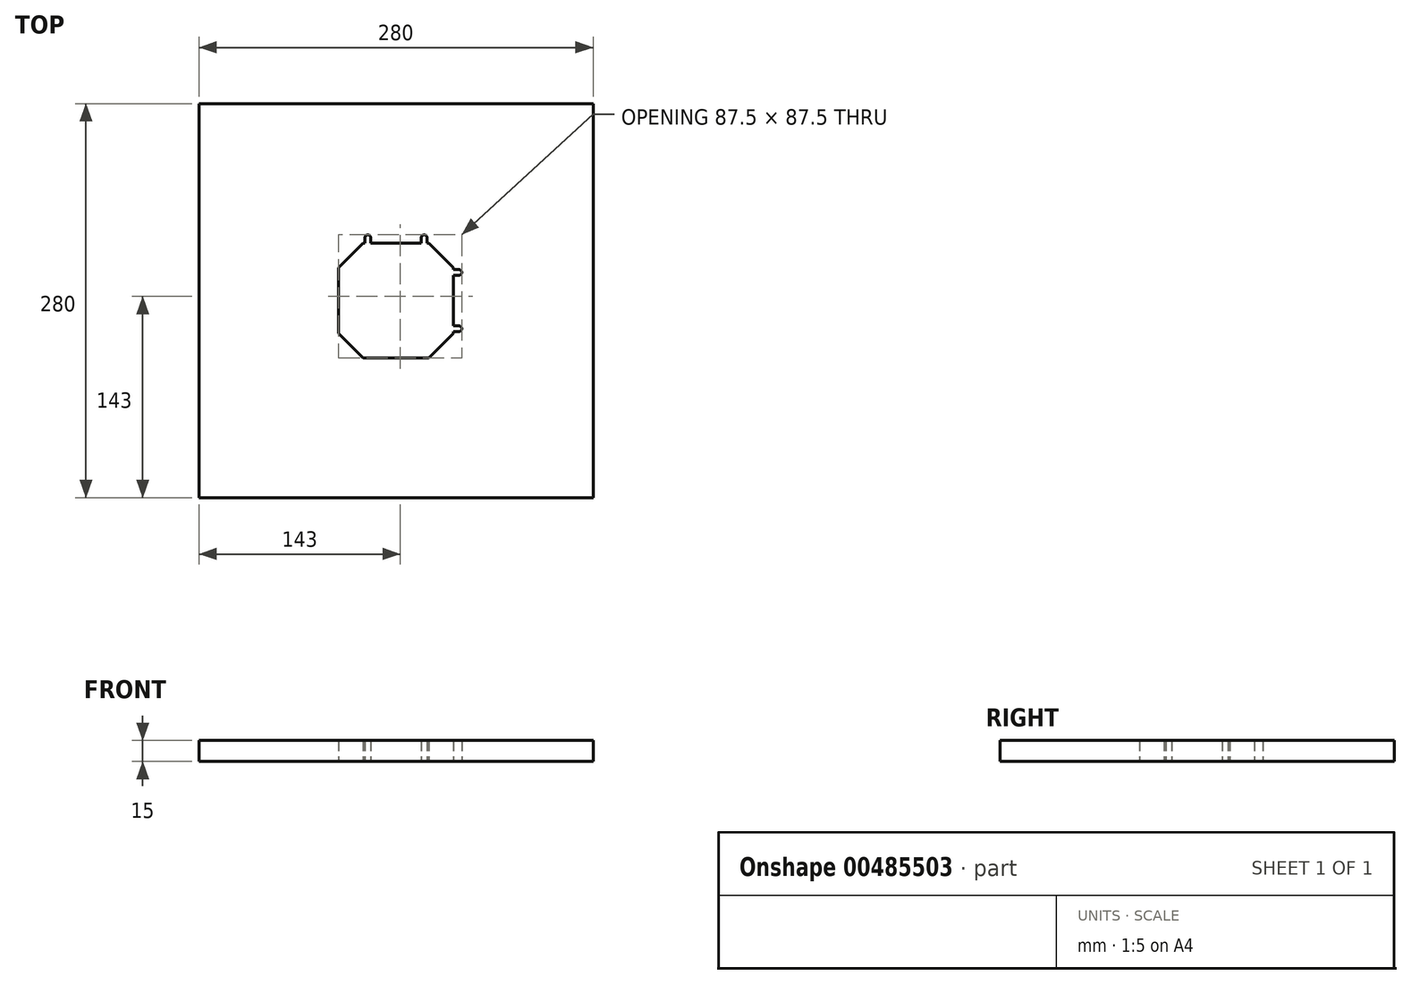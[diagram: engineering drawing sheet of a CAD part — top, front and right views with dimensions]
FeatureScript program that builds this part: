
annotation { "Feature Type Name" : "Feature", "Feature Type Description" : "" }
export const myFeature = defineFeature(function(context is Context, id is Id, definition is map)
    precondition{}
    {
        {
            var Q0;
            Q0=qCreatedBy(makeId("Top.planeOp"),FACE);
            var sketch = newSketch(context, id + "F0", { "sketchPlane" : qUnion([Q0])});
            skLineSegment(sketch, "E0.bottom", {"start": v(-140, 140) * mm, "end": v(140, 140) * mm});
            skLineSegment(sketch, "E0.top", {"start": v(-140, -140) * mm, "end": v(140, -140) * mm});
            skLineSegment(sketch, "E0.left", {"start": v(-140, 140) * mm, "end": v(-140, -140) * mm});
            skLineSegment(sketch, "E0.right", {"start": v(140, 140) * mm, "end": v(140, -140) * mm});
            skPoint(sketch, "E0.middle", {"position": v(0, 0) * mm});
            skSolve(sketch);
        }
        {
            var Q0;
            Q0 = qSketchRegion(id + "F0", true);
            extrude(context, id + "F1", {"entities" : qUnion([Q0]), "depth" : 15 * mm});
        }
        {
            var Q0;
            Q0=qCreatedBy(makeId("Top.planeOp"),FACE);
            var sketch = newSketch(context, id + "F2", { "sketchPlane" : qUnion([Q0])});
            skLineSegment(sketch, "E1.bottom", {"start": v(-40.75, 40.75) * mm, "end": v(40.75, 40.75) * mm, "construction": true});
            skLineSegment(sketch, "E1.top", {"start": v(-40.75, -40.75) * mm, "end": v(40.75, -40.75) * mm, "construction": true});
            skLineSegment(sketch, "E1.left", {"start": v(-40.75, 40.75) * mm, "end": v(-40.75, -40.75) * mm, "construction": true});
            skLineSegment(sketch, "E1.right", {"start": v(40.75, 40.75) * mm, "end": v(40.75, -40.75) * mm, "construction": true});
            skPoint(sketch, "E1.middle", {"position": v(0, 0) * mm});
            skSolve(sketch);
        }
        {
            var Q0;
            Q0=qCreatedBy(makeId("Top.planeOp"),FACE);
            var sketch = newSketch(context, id + "F3", { "sketchPlane" : qUnion([Q0])});
            skLineSegment(sketch, "E2", {"start": v(-40.75, 0) * mm, "end": v(-40.75, 23.25) * mm});
            skLineSegment(sketch, "E3", {"start": v(-40.75, 23.25) * mm, "end": v(-23.25, 40.75) * mm});
            skLineSegment(sketch, "E4", {"start": v(-23.25, 40.75) * mm, "end": v(-22, 40.75) * mm});
            skLineSegment(sketch, "E5", {"start": v(0, 40.75) * mm, "end": v(18, 40.75) * mm});
            skLineSegment(sketch, "E6", {"start": v(23.25, 40.75) * mm, "end": v(40.75, 23.25) * mm});
            skLineSegment(sketch, "E7", {"start": v(40.75, 23.25) * mm, "end": v(40.75, 22) * mm});
            skLineSegment(sketch, "E8", {"start": v(40.75, 0) * mm, "end": v(40.75, -18) * mm});
            skLineSegment(sketch, "E9", {"start": v(40.75, -23.25) * mm, "end": v(23.25, -40.75) * mm});
            skLineSegment(sketch, "E10", {"start": v(23.25, -40.75) * mm, "end": v(0, -40.75) * mm});
            skLineSegment(sketch, "E11", {"start": v(0, -40.75) * mm, "end": v(-23.25, -40.75) * mm});
            skLineSegment(sketch, "E12", {"start": v(-23.25, -40.75) * mm, "end": v(-40.75, -23.25) * mm});
            skLineSegment(sketch, "E13", {"start": v(-40.75, -23.25) * mm, "end": v(-40.75, 0) * mm});
            skLineSegment(sketch, "E14.left", {"start": v(-22, 44.75) * mm, "end": v(-22, 40.75) * mm});
            skLineSegment(sketch, "E14.right", {"start": v(-18, 44.75) * mm, "end": v(-18, 40.75) * mm});
            skPoint(sketch, "E14.middle", {"position": v(-20, 40.75) * mm});
            skLineSegment(sketch, "E15.left", {"start": v(18, 44.75) * mm, "end": v(18, 40.75) * mm});
            skLineSegment(sketch, "E15.right", {"start": v(22, 44.75) * mm, "end": v(22, 40.75) * mm});
            skPoint(sketch, "E15.middle", {"position": v(20, 40.75) * mm});
            skPoint(sketch, "E15.cornerSnap0", {"position": v(-20, 44.75) * mm});
            skArc(sketch, "E16", {"start": v(-18, 44.75) * mm, "mid": v(-20, 46.75) * mm, "end": v(-22, 44.75) * mm});
            skArc(sketch, "E17", {"start": v(22, 44.75) * mm, "mid": v(20, 46.75) * mm, "end": v(18, 44.75) * mm});
            skLineSegment(sketch, "E18.trimOffspring", {"start": v(-18, 40.75) * mm, "end": v(0, 40.75) * mm});
            skLineSegment(sketch, "E19.trimOffspring", {"start": v(22, 40.75) * mm, "end": v(23.25, 40.75) * mm});
            skLineSegment(sketch, "E20.bottom", {"start": v(44.75, 22) * mm, "end": v(40.75, 22) * mm});
            skLineSegment(sketch, "E20.top", {"start": v(44.75, 18) * mm, "end": v(40.75, 18) * mm});
            skPoint(sketch, "E20.middle", {"position": v(40.75, 20) * mm});
            skLineSegment(sketch, "E21.bottom", {"start": v(44.75, -22) * mm, "end": v(40.75, -22) * mm});
            skLineSegment(sketch, "E21.top", {"start": v(44.75, -18) * mm, "end": v(40.75, -18) * mm});
            skPoint(sketch, "E21.middle", {"position": v(40.75, -20) * mm});
            skArc(sketch, "E22", {"start": v(44.75, 18) * mm, "mid": v(46.75, 20) * mm, "end": v(44.75, 22) * mm});
            skArc(sketch, "E23", {"start": v(44.75, -22) * mm, "mid": v(46.75, -20) * mm, "end": v(44.75, -18) * mm});
            skLineSegment(sketch, "E24.trimOffspring", {"start": v(40.75, -22) * mm, "end": v(40.75, -23.25) * mm});
            skPoint(sketch, "E21.right.end.orphan", {"position": v(36.75, -18) * mm});
            skPoint(sketch, "E25.orphan", {"position": v(36.75, -22) * mm});
            skPoint(sketch, "E26.orphan", {"position": v(36.75, 22) * mm});
            skPoint(sketch, "E27.orphan", {"position": v(36.75, 18) * mm});
            skLineSegment(sketch, "E28.trimOffspring", {"start": v(40.75, 18) * mm, "end": v(40.75, 0) * mm});
            skSolve(sketch);
        }
        {
            var Q0;
            Q0 = qSketchRegion(id + "F3", true);
            extrude(context, id + "F4", {"entities" : qUnion([Q0]), "operationType" : NewBodyOperationType.REMOVE, "endBound" : BoundingType.THROUGH_ALL, "depth" : 25 * mm});
        }
        {
            var Q0;
            Q0=makeQuery(id+"F1.opExtrude","CAP_FACE",FACE,{"disambiguationData":[OSD([sQuery(id+"F0.wireOp",EDGE,"E0.bottom"),sQuery(id+"F0.wireOp",EDGE,"E0.top"),sQuery(id+"F0.wireOp",EDGE,"E0.left"),sQuery(id+"F0.wireOp",EDGE,"E0.right")])],"isStart":false});
            var sketch = newSketch(context, id + "F5", { "sketchPlane" : qUnion([Q0])});
            skLineSegment(sketch, "E29.bottom", {"start": v(42, 42) * mm, "end": v(-42, 42) * mm, "construction": true});
            skLineSegment(sketch, "E29.top", {"start": v(42, -42) * mm, "end": v(-42, -42) * mm, "construction": true});
            skLineSegment(sketch, "E29.left", {"start": v(42, 42) * mm, "end": v(42, -42) * mm, "construction": true});
            skLineSegment(sketch, "E29.right", {"start": v(-42, 42) * mm, "end": v(-42, -42) * mm, "construction": true});
            skPoint(sketch, "E29.middle", {"position": v(0, 0) * mm});
            skLineSegment(sketch, "E30.0", {"start": v(-26.36, 43.86) * mm, "end": v(-43.86, 26.36) * mm, "construction": true});
            skLineSegment(sketch, "E31", {"start": v(-42, 42) * mm, "end": v(-35.11, 35.11) * mm, "construction": true});
            skSolve(sketch);
        }
        {
            var Q0;
            {var subQ3=sQuery(id+"F0.wireOp",EDGE,"E0.bottom");Q0=makeQuery(id+"F5.imprint","IMPRINT",FACE,{"disambiguationData":[TD([[makeQuery(id+"F5.imprint","IMPRINT",EDGE,{"derivedFrom":makeQuery(id+"F1.opExtrude","CAP_EDGE",EDGE,{"disambiguationData":[OSD([subQ3])],"isStart":false})}),-1.0]])]});}
            var sketch = newSketch(context, id + "F6", { "sketchPlane" : qUnion([Q0])});
            skPoint(sketch, "E32.0", {"position": v(-38.56, 38.56) * mm});
            skCircle(sketch, "E33", {"center": v(-38.56, 38.56) * mm, "radius": 3 * mm});
            skCircle(sketch, "E34.1.0", {"center": v(-38.56, -38.56) * mm, "radius": 3 * mm});
            skCircle(sketch, "E34.2.0", {"center": v(38.56, -38.56) * mm, "radius": 3 * mm});
            skCircle(sketch, "E34.3.0", {"center": v(38.56, 38.56) * mm, "radius": 3 * mm});
            skPoint(sketch, "E34.center", {"position": v(0, 0) * mm});
            skSolve(sketch);
        }
    });
